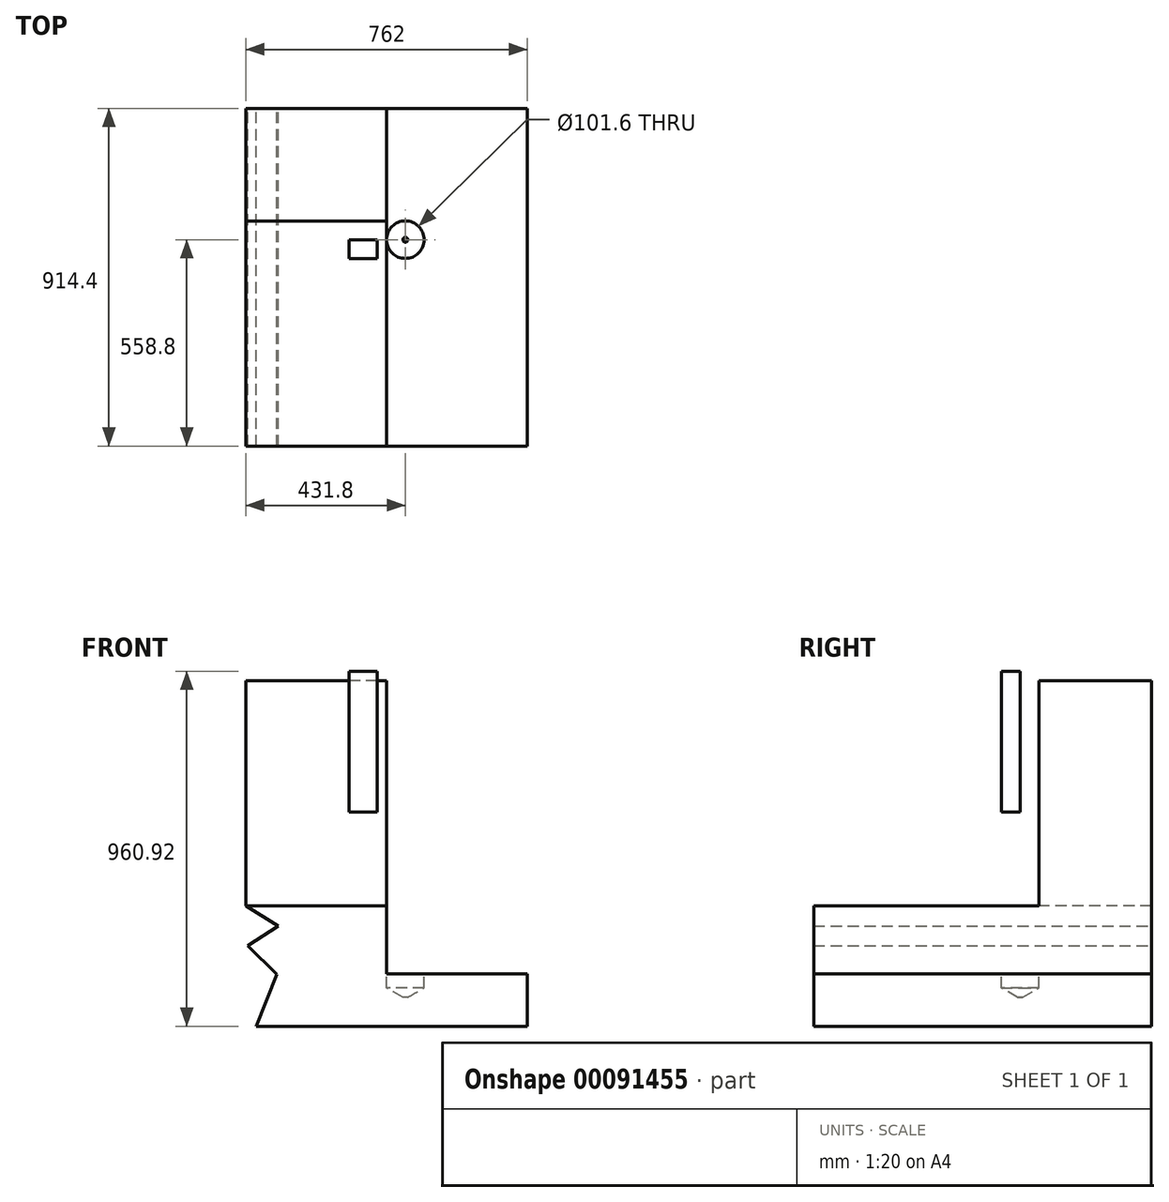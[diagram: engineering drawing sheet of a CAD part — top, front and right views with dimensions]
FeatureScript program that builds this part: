
annotation { "Feature Type Name" : "Feature", "Feature Type Description" : "" }
export const myFeature = defineFeature(function(context is Context, id is Id, definition is map)
    precondition{}
    {
        {
            var Q0;
            Q0=qCreatedBy(makeId("Front.planeOp"),FACE);
            var sketch = newSketch(context, id + "F0", { "sketchPlane" : qUnion([Q0])});
            skLineSegment(sketch, "E0", {"start": v(0, 0) * mm, "end": v(-381, 0) * mm});
            skLineSegment(sketch, "E1", {"start": v(0, 0) * mm, "end": v(0, -184.15) * mm});
            skLineSegment(sketch, "E2", {"start": v(0, -184.15) * mm, "end": v(381, -184.15) * mm});
            skLineSegment(sketch, "E3", {"start": v(381, -184.15) * mm, "end": v(381, -325.92) * mm});
            skLineSegment(sketch, "E4", {"start": v(381, -325.92) * mm, "end": v(-353.14, -325.92) * mm});
            skLineSegment(sketch, "E5", {"start": v(-353.14, -325.92) * mm, "end": v(-297.42, -185.46) * mm});
            skLineSegment(sketch, "E6", {"start": v(-297.42, -185.46) * mm, "end": v(-376.36, -107.7) * mm});
            skLineSegment(sketch, "E7", {"start": v(-376.36, -107.7) * mm, "end": v(-292.78, -54.3) * mm});
            skLineSegment(sketch, "E8", {"start": v(-292.78, -54.3) * mm, "end": v(-381, 0) * mm});
            skLineSegment(sketch, "E9", {"start": v(0, -184.15) * mm, "end": v(0, -325.92) * mm});
            skLineSegment(sketch, "E10", {"start": v(0, 0) * mm, "end": v(0, 609.6) * mm});
            skLineSegment(sketch, "E11", {"start": v(0, 609.6) * mm, "end": v(-381, 609.6) * mm});
            skLineSegment(sketch, "E12", {"start": v(-381, 609.6) * mm, "end": v(-381, 0) * mm});
            skSolve(sketch);
        }
        {
            var Q0;
            Q0=makeQuery(id+"F0.imprint","IMPRINT",FACE,{"disambiguationData":[TD([[makeQuery(id+"F0.imprint","IMPRINT",EDGE,{"derivedFrom":sQuery(id+"F0.wireOp",EDGE,"E0")}),1.0]])]});
            var Q1;
            Q1=makeQuery(id+"F0.imprint","IMPRINT",FACE,{"disambiguationData":[TD([[makeQuery(id+"F0.imprint","IMPRINT",EDGE,{"derivedFrom":sQuery(id+"F0.wireOp",EDGE,"E2")}),-1.0]])]});
            extrude(context, id + "F1", {"entities" : qUnion([Q0, Q1]), "depth" : 609.6 * mm});
        }
        {
            var Q0;
            Q0=makeQuery(id+"F0.imprint","IMPRINT",FACE,{"disambiguationData":[TD([[makeQuery(id+"F0.imprint","IMPRINT",EDGE,{"derivedFrom":sQuery(id+"F0.wireOp",EDGE,"E0")}),1.0]])]});
            var Q1;
            Q1=makeQuery(id+"F0.imprint","IMPRINT",FACE,{"disambiguationData":[TD([[makeQuery(id+"F0.imprint","IMPRINT",EDGE,{"derivedFrom":sQuery(id+"F0.wireOp",EDGE,"E2")}),-1.0]])]});
            var Q2;
            Q2=makeQuery(id+"F0.imprint","IMPRINT",FACE,{"disambiguationData":[TD([[makeQuery(id+"F0.imprint","IMPRINT",EDGE,{"derivedFrom":sQuery(id+"F0.wireOp",EDGE,"E0")}),-1.0]])]});
            extrude(context, id + "F2", {"entities" : qUnion([Q0, Q1, Q2]), "operationType" : NewBodyOperationType.ADD, "oppositeDirection" : true, "depth" : 304.8 * mm});
        }
        {
            var Q0;
            Q0=qCreatedBy(makeId("Top.planeOp"),FACE);
            cPlane(context, id + "F3", {"entities" : qUnion([Q0]), "cplaneType" : CPlaneType.OFFSET, "offset" : 254 * mm, "width" : 152.4 * mm, "height" : 152.4 * mm});
        }
        {
            var Q0;
            Q0=qCreatedBy(id+"F3.planeOp",FACE);
            var sketch = newSketch(context, id + "F4", { "sketchPlane" : qUnion([Q0])});
            skLineSegment(sketch, "E13.bottom", {"start": v(-25.4, -50.8) * mm, "end": v(-101.6, -50.8) * mm});
            skLineSegment(sketch, "E13.top", {"start": v(-25.4, -101.6) * mm, "end": v(-101.6, -101.6) * mm});
            skLineSegment(sketch, "E13.left", {"start": v(-25.4, -50.8) * mm, "end": v(-25.4, -101.6) * mm});
            skLineSegment(sketch, "E13.right", {"start": v(-101.6, -50.8) * mm, "end": v(-101.6, -101.6) * mm});
            skPoint(sketch, "E13.middle", {"position": v(-63.5, -76.2) * mm});
            skSolve(sketch);
        }
        {
            var Q0;
            Q0 = qSketchRegion(id + "F4", true);
            extrude(context, id + "F5", {"entities" : qUnion([Q0]), "depth" : 381 * mm});
        }
        {
            var Q0;
            {var subQ0=sQuery(id+"F0.wireOp",EDGE,"E2");Q0=makeQuery(id+"F2.boolean.opBoolean","MERGE",FACE,{"derivedFrom":[makeQuery(id+"F1.opExtrude","SWEPT_FACE",FACE,{"disambiguationData":[OSD([subQ0])]}),makeQuery(id+"F2.opExtrude","SWEPT_FACE",FACE,{"disambiguationData":[OSD([subQ0])]})]});}
            var sketch = newSketch(context, id + "F6", { "sketchPlane" : qUnion([Q0])});
            skCircle(sketch, "E14", {"center": v(50.8, -50.8) * mm, "radius": 50.8 * mm});
            skSolve(sketch);
        }
        {
            var Q0;
            Q0=makeQuery(id+"F6.imprint","IMPRINT",FACE,{"disambiguationData":[TD([[makeQuery(id+"F6.imprint","IMPRINT",EDGE,{"derivedFrom":sQuery(id+"F6.wireOp",EDGE,"E14")}),1.0]])]});
            var Q1;
            Q1=sQuery(id+"F6.wireOp",EDGE,"E14");
            extrude(context, id + "F7", {"entities" : qUnion([Q0]), "operationType" : NewBodyOperationType.REMOVE, "surfaceEntities" : qUnion([Q1]), "oppositeDirection" : true, "depth" : 38.1 * mm});
        }
        {
            var Q0;
            Q0=makeQuery(id+"F7.boolean.opBoolean","COPY",FACE,{"derivedFrom":makeQuery(id+"F7.opExtrude","CAP_FACE",FACE,{"disambiguationData":[OSD([sQuery(id+"F6.wireOp",EDGE,"E14")])],"isStart":false})});
            var sketch = newSketch(context, id + "F8", { "sketchPlane" : qUnion([Q0])});
            skCircle(sketch, "E15", {"center": v(50.8, -50.8) * mm, "radius": 50.8 * mm});
            skSolve(sketch);
        }
        {
            var Q0;
            Q0=makeQuery(id+"F8.imprint","IMPRINT",FACE,{"disambiguationData":[TD([[makeQuery(id+"F8.imprint","IMPRINT",EDGE,{"derivedFrom":sQuery(id+"F8.wireOp",EDGE,"E15")}),1.0]])]});
            extrude(context, id + "F9", {"entities" : qUnion([Q0]), "operationType" : NewBodyOperationType.REMOVE, "oppositeDirection" : true, "depth" : 25.4 * mm, "hasDraft" : true, "draftAngle" : 60 * degree, "draftPullDirection" : true});
        }
        {
            var Q0;
            Q0=qCreatedBy(makeId("Front.planeOp"),FACE);
            cPlane(context, id + "F10", {"entities" : qUnion([Q0]), "cplaneType" : CPlaneType.OFFSET, "offset" : 50.8 * mm, "width" : 152.4 * mm, "height" : 152.4 * mm});
        }
    });
